# Revit family: Camera-Security-Panasonic-FullHD_Rugged_Mobile_Network-SBV131M_111MX
name_source: partatom
category: Security Devices
revit_build: Autodesk Revit 2013 (Build: 20130531_2115(x64)
units: mm (PartAtom-declared; Revit-internal decimal feet)

## types (2) — shared parameters
Alarm Input Or Output Specification = No
Audio In = No
Audio Out = No
Communication Ports = 10Base-T / 100Base-TX, M12 connector (female)
Date Last Modified = January, 31, 2017
Day Or Night = Yes
Depth = 6.339 "
Equipment Abbreviation = SC
Family Version = 1.0.0
Has POE = Yes
Height = 3.15 "
IP Or Analog = IP
Impact Protection = Compliant with IK10 (IEC 62262)
Indoor Or Outdoor = Outdoor
Manufacturer = Panasonic
Minimum Illumination = 0 lx
Model Disclaimer = Contact Panasonic for more information
Mounting Positions = Surface Mount
Operational Humidity = 10% to 90% (no condensation)
Operational Temperature = -40°F - 140°F
Pan Max = 170.00°
Pan Min = -170.00°
Panning Range = -170 to +170
Power Active = 3.8 W
Product Documentation Link = http://ssbu-t.psn-web.net
Product Material = Paint - Panasonic - Sail White
Product Page URL = http://security.panasonic.com
Provide Feedback = https://www.surveymonkey.com
Regulatory Compliance = UL60950-1, C-UL CAN/CSA C22.2 No.60950-1, CE, IEC60950-1 FCC Part15 ClassA, ICES003 ClassA, EN55022 ClassB, EN55024
Storage Temperature = -40°F - 149°F
Tilt Max = 90.00°
Tilt Min = -90.00°
Tilting Range = -90 to +90
URL = http://security.panasonic.com
Vandal Resistant = Yes
Voltage DC = 48 V
Water and Dust Resistance = IP66 (IEC60529), IP6K9K, Type 4X (UL50), NEMA 4X compliant
Wide Dynamic Range = Yes
Width = 3.937 "
Yaw Max = 170.00°
Yaw Min = -170.00°
z Const Pan Handle Length = 27.559 "
z Const Tilt Base Length = 9.843 "
z Const Tilt Base2 Length = 19.685 "
z Const Tilt Handle Length = 14.173 "
z Const Yaw Base Length = 10.236 "
z Const Yaw Base2 Length = 17.323 "
z Const Yaw Handle Length = 9.252 "
zero-valued in all types: Default Elevation, z VV Viewpoint Depth Max, z VV Viewpoint Depth Min

## per-type parameters (varying)
| type | Angle Of View | Description | HFOV Max 169 | HFOV Max 43 | HFOV Min 169 | HFOV Min 43 | Model | Part Description | Part Number | VFOV Max 169 | VFOV Max 43 | VFOV Min 169 | VFOV Min 43 | z Camera Resolution Type |
| Full HD, WV-SBV131M | 97 | Security Camera, Full HD, Rugged, Mobile, Network, SBV131M | 109.00° | 97.00° | 109.00° | 97.00° | WV-SBV131M | Security Camera, Full HD, Rugged, Mobile, Network, SBV131M | WV-SBV131M | 73.00° | 79.00° | 73.00° | 79.00° | 1 |
| HD, WV-SBV111M | 104 | Security Camera, HD, Rugged, Mobile, Network, SBV111M | 104.00° | 104.00° | 104.00° | 104.00° | WV-SBV111M | Security Camera, HD, Rugged, Mobile, Network, SBV111M | WV-SBV111M | 69.00° | 85.00° | 69.00° | 85.00° | 2 |

## geometry (parser evidence)
native form markers: Sweep x3
no freeform markers — native parametric forms only
